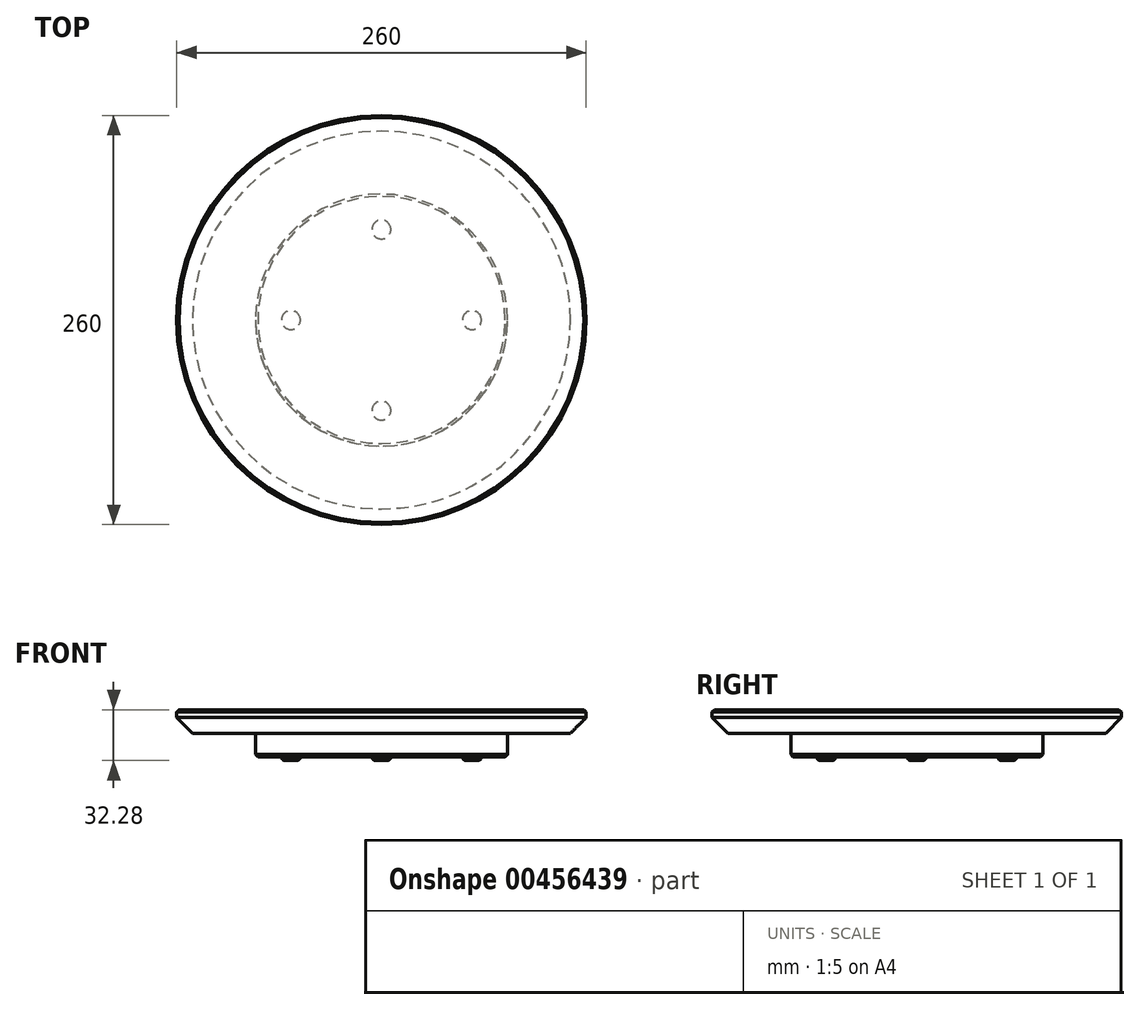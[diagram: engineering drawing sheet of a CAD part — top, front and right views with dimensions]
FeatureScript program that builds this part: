
annotation { "Feature Type Name" : "Feature", "Feature Type Description" : "" }
export const myFeature = defineFeature(function(context is Context, id is Id, definition is map)
    precondition{}
    {
        {
            var Q0;
            Q0=qCreatedBy(makeId("Front.planeOp"),FACE);
            var sketch = newSketch(context, id + "F0", { "sketchPlane" : qUnion([Q0])});
            skLineSegment(sketch, "E0", {"start": v(0, 0) * mm, "end": v(0, 15) * mm});
            skLineSegment(sketch, "E1", {"start": v(0, 15) * mm, "end": v(-80, 15) * mm});
            skLineSegment(sketch, "E2", {"start": v(-80, 15) * mm, "end": v(-80, 0) * mm});
            skLineSegment(sketch, "E3", {"start": v(-80, 0) * mm, "end": v(0, 0) * mm});
            skSolve(sketch);
        }
        {
            var Q0;
            Q0=makeQuery(id+"F0.imprint","IMPRINT",FACE,{"disambiguationData":[TD([[makeQuery(id+"F0.imprint","IMPRINT",EDGE,{"derivedFrom":sQuery(id+"F0.wireOp",EDGE,"E0")}),1.0]])]});
            var Q1;
            Q1=sQuery(id+"F0.wireOp",EDGE,"E0");
            revolve(context, id + "F1", {"entities" : qUnion([Q0]), "axis" : qUnion([Q1]), "revolveType" : RevolveType.FULL});
        }
        {
            var Q0;
            Q0=qCreatedBy(makeId("Front.planeOp"),FACE);
            var sketch = newSketch(context, id + "F2", { "sketchPlane" : qUnion([Q0])});
            skLineSegment(sketch, "E4", {"start": v(0, 15) * mm, "end": v(-120, 15) * mm});
            skLineSegment(sketch, "E5", {"start": v(-120, 15) * mm, "end": v(-130, 25) * mm});
            skLineSegment(sketch, "E6", {"start": v(-130, 25) * mm, "end": v(-130, 30) * mm});
            skLineSegment(sketch, "E7", {"start": v(-130, 30) * mm, "end": v(0, 30) * mm});
            skLineSegment(sketch, "E8", {"start": v(0, 30) * mm, "end": v(0, 15) * mm});
            skSolve(sketch);
        }
        {
            var Q0;
            Q0 = qSketchRegion(id + "F2", true);
            var Q1;
            Q1=sQuery(id+"F2.wireOp",EDGE,"E8");
            revolve(context, id + "F3", {"entities" : qUnion([Q0]), "axis" : qUnion([Q1]), "revolveType" : RevolveType.FULL});
        }
        {
            var Q0;
            Q0=makeQuery(id+"F3.opRevolve","SWEPT_EDGE",EDGE,{"disambiguationData":[OSD([sQuery(id+"F2.wireOp",EDGE,"E6"),sQuery(id+"F2.wireOp",EDGE,"E7")])]});
            chamfer(context, id + "F4", {"entities" : qUnion([Q0]), "width" : 1.5 * mm, "tangentPropagation" : true});
        }
        {
            var Q0;
            Q0=makeQuery(id+"F1.opRevolve","SWEPT_EDGE",EDGE,{"disambiguationData":[OSD([sQuery(id+"F0.wireOp",EDGE,"E2"),sQuery(id+"F0.wireOp",EDGE,"E3")])]});
            chamfer(context, id + "F5", {"entities" : qUnion([Q0]), "width" : 1.5 * mm, "tangentPropagation" : true});
        }
        {
            var Q0;
            Q0=qCreatedBy(makeId("Front.planeOp"),FACE);
            var sketch = newSketch(context, id + "F6", { "sketchPlane" : qUnion([Q0])});
            skLineSegment(sketch, "E9", {"start": v(57.5, 0) * mm, "end": v(57.5, -2.28) * mm});
            skLineSegment(sketch, "E10", {"start": v(57.5, -2.28) * mm, "end": v(61.22, -2.28) * mm});
            skArc(sketch, "E11", {"start": v(61.22, -2.28) * mm, "mid": v(62.83, -1.61) * mm, "end": v(63.5, 0) * mm});
            skLineSegment(sketch, "E12", {"start": v(63.5, 0) * mm, "end": v(63.5, 1.57) * mm, "construction": true});
            skLineSegment(sketch, "E13", {"start": v(57.5, 0) * mm, "end": v(63.5, 0) * mm});
            skLineSegment(sketch, "E14.0", {"start": v(78.5, 0) * mm, "end": v(-78.5, 0) * mm, "construction": true});
            skSolve(sketch);
        }
        {
            var Q0;
            Q0 = qSketchRegion(id + "F6", true);
            var Q1;
            Q1=sQuery(id+"F6.wireOp",EDGE,"E9");
            revolve(context, id + "F7", {"entities" : qUnion([Q0]), "axis" : qUnion([Q1]), "revolveType" : RevolveType.FULL});
        }
        {
            var Q0;
            Q0=qCreatedBy(makeId("Front.planeOp"),FACE);
            var sketch = newSketch(context, id + "F8", { "sketchPlane" : qUnion([Q0])});
            skLineSegment(sketch, "E15", {"start": v(0, 0) * mm, "end": v(0, -62.71) * mm, "construction": true});
            skSolve(sketch);
        }
        {
            var Q0;
            Q0=makeQuery(id+"F7.opRevolve","SWEPT_BODY",BODY,{"disambiguationData":[OSD([sQuery(id+"F6.wireOp",EDGE,"E9"),sQuery(id+"F6.wireOp",EDGE,"E10"),sQuery(id+"F6.wireOp",EDGE,"E11"),sQuery(id+"F6.wireOp",EDGE,"E13")])]});
            var Q1;
            Q1=sQuery(id+"F8.wireOp",EDGE,"E15");
            circularPattern(context, id + "F9", {"entities" : qUnion([Q0]), "axis" : qUnion([Q1]), "angle" : 360 * degree, "instanceCount" : 4, "equalSpace" : true});
        }
    });
